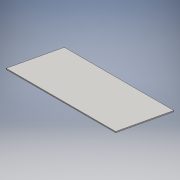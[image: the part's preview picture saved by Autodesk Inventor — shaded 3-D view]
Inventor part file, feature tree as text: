
AUTODESK INVENTOR PART (.ipt)
format: ipt  version: 2016 (Build 200138000, 138)  size: 89,600 bytes
history: native  units: mm
features: other x1, extrude x1, sketch x1
ambient origin geometry x8: Origin, YZ Plane, XZ Plane, XY Plane, X Axis, Y Axis, Z Axis, Center Point
bodies: Body1 (feature_tree)
feature tree (3):
  other  "Bryła1"
  extrude  "Wyciągnięcie proste1"  Depth=1.0mm
  sketch  "Szkic1"
